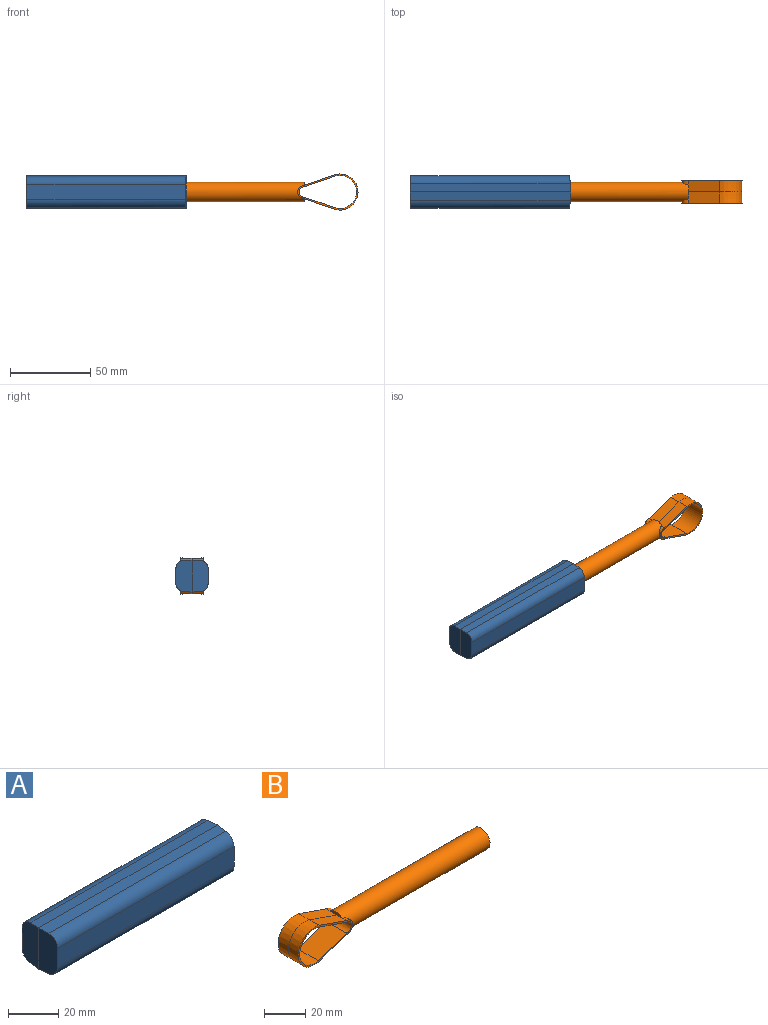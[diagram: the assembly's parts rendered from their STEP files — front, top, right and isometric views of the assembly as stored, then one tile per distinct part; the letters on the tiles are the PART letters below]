
ASSEMBLY  parts=2 mates=1
PART A: 16 faces, bbox 100x20x20 mm
  f0: plane 100x5.26mm, normal (0,-0.05,-1), area 525.4mm2, adj f1,f3,f5,f13
  f1: plane 20x10mm, normal (1,-0.05,0), area 128.9mm2, adj f0,f2,f4,f8,f12,f13,f14
  f2: plane 100x5.26mm, normal (0,-0.05,1), area 525.4mm2, adj f1,f3,f7,f12
  f3: plane 20x10mm, normal (-1,-0.05,0), area 185.5mm2, adj f0,f2,f4,f6,f12,f13
  f4: plane 98.95x9.46mm, normal (0,-1,0), area 936.3mm2, adj f1,f3,f12,f13
  f5: plane 100x5.26mm, normal (0,0.05,-1), area 525.4mm2, adj f0,f6,f8,f11
  f6: plane 20x10mm, normal (-1,0.05,0), area 185.5mm2, adj f3,f5,f7,f9,f10,f11
  f7: plane 100x5.26mm, normal (0,0.05,1), area 525.4mm2, adj f2,f6,f8,f10
  f8: plane 20x10mm, normal (1,0.05,0), area 128.9mm2, adj f1,f5,f7,f9,f10,f11,f14
  f9: plane 98.95x9.46mm, normal (0,1,0), area 936.3mm2, adj f6,f8,f10,f11
  f10: cylinder r=5mm len=99.45mm, axis (1,0,0), area 752.6mm2, adj f6,f7,f8,f9
  f11: cylinder r=5mm len=99.45mm, axis (1,0,0), area 752.6mm2, adj f5,f6,f8,f9
  f12: cylinder r=5mm len=99.45mm, axis (-1,0,0), area 752.6mm2, adj f1,f2,f3,f4
  f13: cylinder r=5mm len=99.45mm, axis (-1,0,0), area 752.6mm2, adj f0,f1,f3,f4
  f14: cylinder r=6mm len=26.5mm, axis (1,0,0), area 991.5mm2, adj f1,f8,f15
  f15: plane 12x12mm, normal (1,0,0), area 113.1mm2, adj f14
PART B: 18 faces, bbox 133.2x14x22.5 mm
  f0: plane 37.49x22.49mm, normal (0,-1,0), area 87.4mm2, adj f6,f7,f8,f9,f14,f15,f16,f17
  f1: plane 37.49x22.49mm, normal (0,1,0), area 87.4mm2, adj f10,f11,f12,f13,f14,f15,f16,f17
  f2: plane 8.65x2mm, normal (-1,0,0), area 11.7mm2, adj f3,f7,f11
  f3: cylinder r=6mm len=100mm, axis (-1,0,0), area 3710.9mm2, adj f2,f4,f5,f6,f7,f8,f10,f11
  f4: plane 8.65x2mm, normal (-1,0,0), area 11.7mm2, adj f3,f8,f12
  f5: plane 12x12mm, normal (1,0,0), area 113.1mm2, adj f3
  f6: cone r=4mm half-angle=2deg, axis (0,-1,0), area 23.7mm2, adj f0,f3,f7,f8
  f7: plane 18.89x7mm, normal (0.33,0.03,0.94), area 139.6mm2, adj f0,f2,f3,f6,f9,f11
  f8: plane 19.38x7mm, normal (0.33,0.03,-0.94), area 143.1mm2, adj f0,f3,f4,f6,f9,f12
  f9: cone r=11mm half-angle=2deg, axis (0,-1,0), area 286.5mm2, adj f0,f7,f8,f13
  f10: cone r=4mm half-angle=2deg, axis (0,1,0), area 23.7mm2, adj f1,f3,f11,f12
  f11: plane 18.89x7mm, normal (0.33,-0.03,0.94), area 139.6mm2, adj f1,f2,f3,f7,f10,f13
  f12: plane 19.38x7mm, normal (0.33,-0.03,-0.94), area 143.1mm2, adj f1,f3,f4,f8,f10,f13
  f13: cone r=11mm half-angle=2deg, axis (0,1,0), area 286.5mm2, adj f1,f9,f11,f12
  f14: cylinder r=10.29mm len=20.59mm, axis (0,1,0), area 529.2mm2, adj f0,f1,f15,f17
  f15: plane 18.95x14mm, normal (-0.33,0,-0.94), area 280.9mm2, adj f0,f1,f14,f16
  f16: cylinder r=3.29mm len=14mm, axis (0,1,0), area 148.1mm2, adj f0,f1,f15,f17
  f17: plane 19.43x14mm, normal (-0.33,0,0.95), area 287.7mm2, adj f0,f1,f14,f16
PLACE A t=(-12.85,-22.6,10.52)mm
PLACE B rot(axis=(0,1,0),180deg) t=(60.65,-22.6,20.52)mm
MATE planar B.f3 <-> A.f14  axis (-1,0,0) through (-39.35,-22.6,20.52)mm
